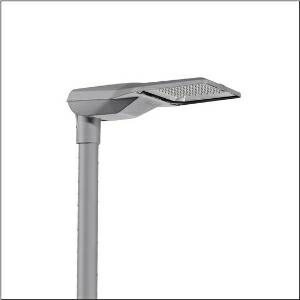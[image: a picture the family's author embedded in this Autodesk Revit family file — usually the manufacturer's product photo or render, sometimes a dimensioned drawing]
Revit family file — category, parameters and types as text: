
# Revit family: streetlight_sl_21_iq_midi___p0_8a_5xe3u31d08mb_ad50
name_source: partatom
category: Lighting Fixtures
units: mm (PartAtom-declared; Revit-internal decimal feet)

## family parameters
Cut with Voids When Loaded = No
Host = Face
Light Source = No
Part Type = Normal
Room Calculation Point = No
Round Connector Dimension = Use Diameter
Shared = No

## types (1)
- --- (1 x LED, 19670 lm, 146.7 W, 3000K)
    Apparent Load = 147 VA
    CIE Flux Codes = 33 69 96 100 100
    Color Rendering = 70
    Color Temperature = 3000K
    Default Elevation = 1800 mm
    Description = Streetlight SL 21 iQ midi, mast luminaire, primary light control with lens, of PMMA, primary optical cover: cover, of toughened safety glass, transparent, light distribution: P0.8a, light emission: direct distribution, primary light characteristic: asymmetric, installation type: post-top, side-entry, LED, High Power LED, rated luminous flux: 19.670lm, luminous efficacy: 134lm/W, light colour: 730, colour temperature: 3000K, control gear: iQ-Comfort, control: pre-setting: linear dimming characteristic, Auto-Match, Temp-Guard, Lumen-Switch, Night-Set, Smart-Wire, Light-Fading, Desk-Remote (wireless, voltage-free reading and setting of iQ features in the workshop via application-optimized NFC function/RFID function), optimised constant luminous flux control (CLO 2.0), mains connection: 230..240V, AC, 50/60Hz, start of lifetime: 147W, end of service life: 161W, reduction: 62W, luminaire housing, of diecast aluminium, powder-coated, SITECO metallic grey (DB 702S), corrosivity category C5 high according to DIN EN ISO 12944, please order mast flange separately, inclination adjustable: 0°, 5°, 10°, 15°, sealing non-destructively replaceable, multi-level sealing system, length: 644mm, width: 335mm, height: 110mm, mast flange for spigot size: 42mm (side-entry): 5XC10008XM4, 60/48mm (side-entry/post-top): 5XC10108XM2, 76/60mm (side-entry/post-top): 5XC10108XM1, mounting height: 4..8m, protection rating (complete): IP66, insulation class (complete): insulation class II (safety insulation), certification: CE, ENEC, ENEC+, VDE, impact resistance: IK10, permissible operating ambient temperature for outdoor applications: -40..+50°C, standard-compliant lighting for roads and squares, packaging unit: 1 piece

Light Distribution: P0.8a
    Height = 111 mm
    Lamp = 1 x LED
    Lamp Light Flux = 19670 lm
    Lamp Power = 146.7 W
    Lamp count = 1
    Length = 644 mm
    Luminous efficacy = 134 lm/W
    Manufacturer = Siteco
    ModVariant = No
    Model = 5XE3U31D08MB
    Number of Poles = 1
    OnlyDefault = Yes
    Power Factor = 1
    Product Name = Streetlight SL 21 iQ midi | P0.8a
    Product group = mast luminaire | pylon top
    ProductGroupID = 6100
    Protection Class = Protection class II
    Protection Degree = IP 66
    RLX_Detail_Level = 1
    RLX_Emergency_Light_Flux = 0 lm
    RLX_Emergency_Type = 0
    RLX_Emergency_Type_DB = No
    RlxData = <blob elided: 90389 chars, md5=fcd72085>
    Socket = socket
    Standby Power = 0 W
    System Light Flux = 19670 lm
    System Power = 147 W
    Type Comments = factory setting: luminous flux: 100 % | dim-lin: 254 | 753 mA
    Type Image = l_1004298.jpg
    URL = http://relux.com
    VarID = @adj_080105
    Voltage = 0 V
    Weight = 0.00 kg
    Width = 336 mm

## geometry (parser evidence)
native form markers: Blend x4, Sweep x10
no freeform markers — native parametric forms only
